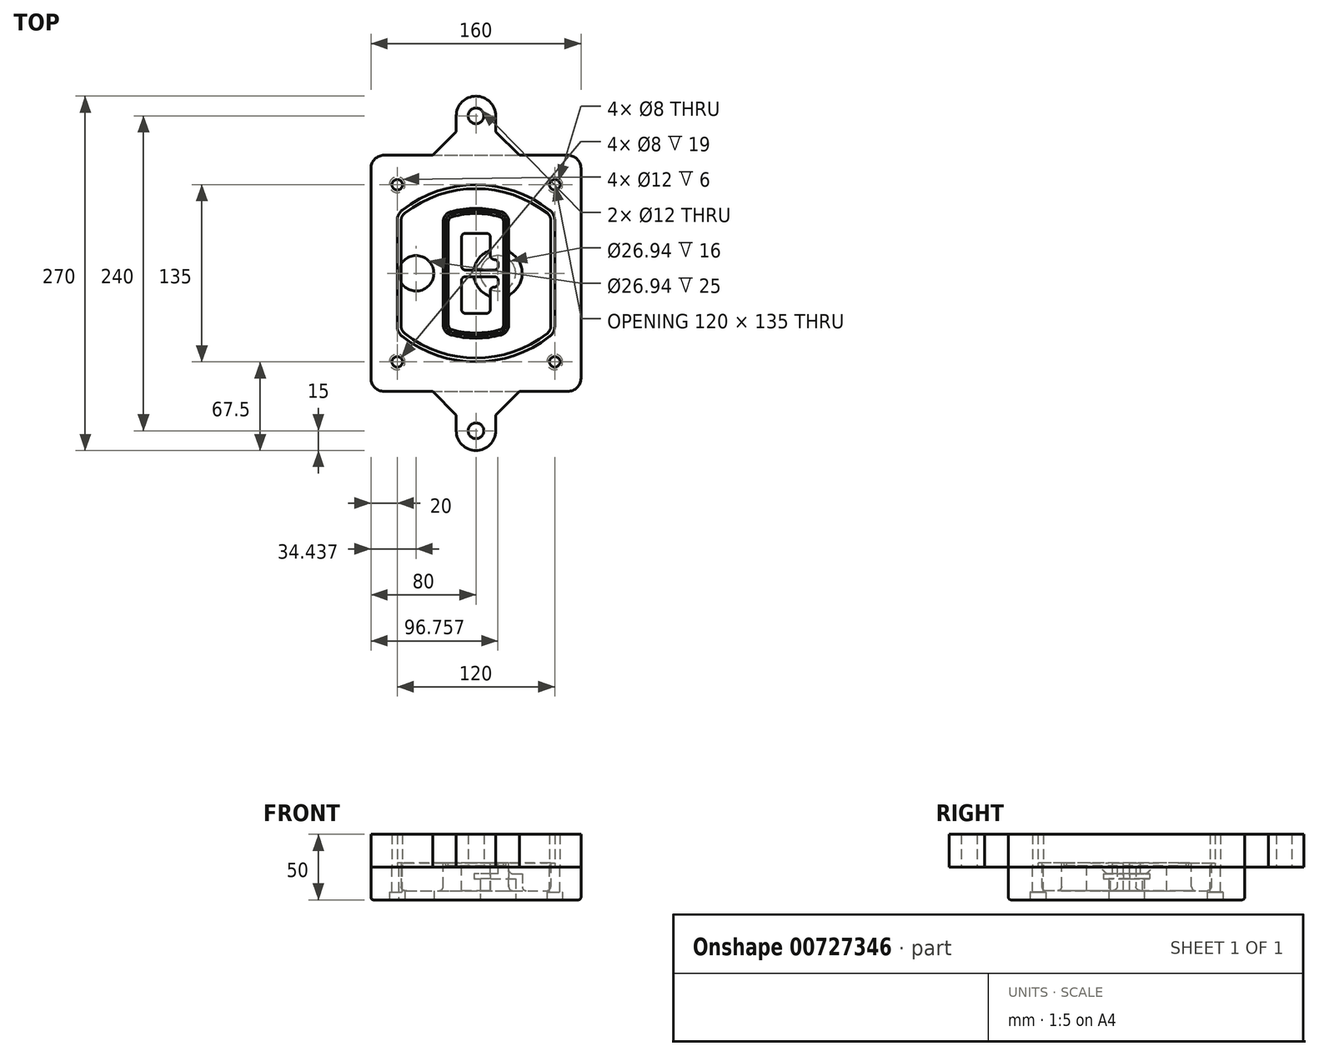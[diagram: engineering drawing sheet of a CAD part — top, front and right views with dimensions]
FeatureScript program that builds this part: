
annotation { "Feature Type Name" : "Feature", "Feature Type Description" : "" }
export const myFeature = defineFeature(function(context is Context, id is Id, definition is map)
    precondition{}
    {
        {
            var Q0;
            Q0=qCreatedBy(makeId("Top.planeOp"),FACE);
            var sketch = newSketch(context, id + "F0", { "sketchPlane" : qUnion([Q0])});
            skPoint(sketch, "E0.rect.middle", {"position": v(0, 0) * mm});
            skLineSegment(sketch, "E1.bottom", {"start": v(-70, -90) * mm, "end": v(70, -90) * mm});
            skLineSegment(sketch, "E1.top", {"start": v(-70, 90) * mm, "end": v(70, 90) * mm});
            skLineSegment(sketch, "E1.left", {"start": v(-80, -80) * mm, "end": v(-80, 80) * mm});
            skLineSegment(sketch, "E1.right", {"start": v(80, -80) * mm, "end": v(80, 80) * mm});
            skLineSegment(sketch, "E2", {"start": v(-80, 90) * mm, "end": v(80, -90) * mm, "construction": true});
            skLineSegment(sketch, "E3", {"start": v(80, 90) * mm, "end": v(-80, -90) * mm, "construction": true});
            skCircle(sketch, "E4", {"center": v(-60, 67.5) * mm, "radius": 4 * mm});
            skCircle(sketch, "E5", {"center": v(60, 67.5) * mm, "radius": 4 * mm});
            skCircle(sketch, "E6", {"center": v(60, -67.5) * mm, "radius": 4 * mm});
            skCircle(sketch, "E7", {"center": v(-60, -67.5) * mm, "radius": 4 * mm});
            skLineSegment(sketch, "E8", {"start": v(-60, 67.5) * mm, "end": v(60, 67.5) * mm, "construction": true});
            skLineSegment(sketch, "E9", {"start": v(60, 67.5) * mm, "end": v(60, -67.5) * mm, "construction": true});
            skLineSegment(sketch, "E10", {"start": v(60, -67.5) * mm, "end": v(-60, -67.5) * mm, "construction": true});
            skLineSegment(sketch, "E11", {"start": v(-60, -67.5) * mm, "end": v(-60, 67.5) * mm, "construction": true});
            skLineSegment(sketch, "E12", {"start": v(-60, 40.3) * mm, "end": v(-60, -40.3) * mm});
            skLineSegment(sketch, "E13", {"start": v(60, 40.3) * mm, "end": v(60, -40.3) * mm});
            skArc(sketch, "E14", {"start": v(56.15, 48.18) * mm, "mid": v(0, 67.5) * mm, "end": v(-56.15, 48.18) * mm});
            skArc(sketch, "E15", {"start": v(-56.15, -48.18) * mm, "mid": v(0, -67.5) * mm, "end": v(56.15, -48.18) * mm});
            skLineSegment(sketch, "E16", {"start": v(-60, 0) * mm, "end": v(60, 0) * mm, "construction": true});
            skPoint(sketch, "E17.visualSharp", {"position": v(-60, -45) * mm});
            skArc(sketch, "E17.filletArc", {"start": v(-60, -40.3) * mm, "mid": v(-58.99, -44.68) * mm, "end": v(-56.15, -48.18) * mm});
            skPoint(sketch, "E18.visualSharp", {"position": v(-60, 45) * mm});
            skArc(sketch, "E18.filletArc", {"start": v(-56.15, 48.18) * mm, "mid": v(-58.99, 44.68) * mm, "end": v(-60, 40.3) * mm});
            skPoint(sketch, "E19.visualSharp", {"position": v(60, 45) * mm});
            skArc(sketch, "E19.filletArc", {"start": v(60, 40.3) * mm, "mid": v(58.99, 44.68) * mm, "end": v(56.15, 48.18) * mm});
            skPoint(sketch, "E20.visualSharp", {"position": v(60, -45) * mm});
            skArc(sketch, "E20.filletArc", {"start": v(56.15, -48.18) * mm, "mid": v(58.99, -44.68) * mm, "end": v(60, -40.3) * mm});
            skPoint(sketch, "E21.visualSharp", {"position": v(-80, 90) * mm});
            skArc(sketch, "E21.filletArc", {"start": v(-70, 90) * mm, "mid": v(-77.07, 87.07) * mm, "end": v(-80, 80) * mm});
            skPoint(sketch, "E22.visualSharp", {"position": v(80, 90) * mm});
            skArc(sketch, "E22.filletArc", {"start": v(80, 80) * mm, "mid": v(77.07, 87.07) * mm, "end": v(70, 90) * mm});
            skPoint(sketch, "E23.visualSharp", {"position": v(80, -90) * mm});
            skArc(sketch, "E23.filletArc", {"start": v(70, -90) * mm, "mid": v(77.07, -87.07) * mm, "end": v(80, -80) * mm});
            skPoint(sketch, "E24.visualSharp", {"position": v(-80, -90) * mm});
            skArc(sketch, "E24.filletArc", {"start": v(-80, -80) * mm, "mid": v(-77.07, -87.07) * mm, "end": v(-70, -90) * mm});
            skArc(sketch, "E25.0", {"start": v(57, 40.3) * mm, "mid": v(56.3, 43.36) * mm, "end": v(54.3, 45.81) * mm});
            skLineSegment(sketch, "E25.1", {"start": v(57, 40.3) * mm, "end": v(57, -40.3) * mm});
            skArc(sketch, "E25.2", {"start": v(54.3, -45.81) * mm, "mid": v(56.3, -43.36) * mm, "end": v(57, -40.3) * mm});
            skArc(sketch, "E25.3", {"start": v(-54.3, -45.81) * mm, "mid": v(0, -64.5) * mm, "end": v(54.3, -45.81) * mm});
            skArc(sketch, "E25.4", {"start": v(-57, -40.3) * mm, "mid": v(-56.3, -43.36) * mm, "end": v(-54.3, -45.81) * mm});
            skArc(sketch, "E25.5", {"start": v(54.3, 45.81) * mm, "mid": v(0, 64.5) * mm, "end": v(-54.3, 45.81) * mm});
            skLineSegment(sketch, "E25.6", {"start": v(-57, 40.3) * mm, "end": v(-57, -40.3) * mm});
            skArc(sketch, "E25.7", {"start": v(-54.3, 45.81) * mm, "mid": v(-56.3, 43.36) * mm, "end": v(-57, 40.3) * mm});
            skArc(sketch, "E26.0", {"start": v(-58.62, 51.33) * mm, "mid": v(-62.58, 46.43) * mm, "end": v(-64, 40.3) * mm});
            skArc(sketch, "E26.1", {"start": v(58.62, 51.33) * mm, "mid": v(0, 71.5) * mm, "end": v(-58.62, 51.33) * mm});
            skArc(sketch, "E26.2", {"start": v(64, 40.3) * mm, "mid": v(62.58, 46.43) * mm, "end": v(58.62, 51.33) * mm});
            skLineSegment(sketch, "E26.3", {"start": v(64, 40.3) * mm, "end": v(64, -40.3) * mm});
            skArc(sketch, "E26.4", {"start": v(58.62, -51.33) * mm, "mid": v(62.58, -46.43) * mm, "end": v(64, -40.3) * mm});
            skLineSegment(sketch, "E26.5", {"start": v(-64, 40.3) * mm, "end": v(-64, -40.3) * mm});
            skArc(sketch, "E26.6", {"start": v(-58.62, -51.33) * mm, "mid": v(0, -71.5) * mm, "end": v(58.62, -51.33) * mm});
            skArc(sketch, "E26.7", {"start": v(-64, -40.3) * mm, "mid": v(-62.58, -46.43) * mm, "end": v(-58.62, -51.33) * mm});
            skSolve(sketch);
        }
        {
            var Q0;
            Q0=makeQuery(id+"F0.imprint","IMPRINT",FACE,{"disambiguationData":[TD([[makeQuery(id+"F0.imprint","IMPRINT",EDGE,{"derivedFrom":sQuery(id+"F0.wireOp",EDGE,"E1.bottom")}),1.0]])]});
            var Q1;
            Q1=makeQuery(id+"F0.imprint","IMPRINT",FACE,{"disambiguationData":[TD([[makeQuery(id+"F0.imprint","IMPRINT",EDGE,{"derivedFrom":sQuery(id+"F0.wireOp",EDGE,"E12")}),1.0]])]});
            var Q2;
            Q2=makeQuery(id+"F0.imprint","IMPRINT",FACE,{"disambiguationData":[TD([[makeQuery(id+"F0.imprint","IMPRINT",EDGE,{"derivedFrom":sQuery(id+"F0.wireOp",EDGE,"E25.0")}),1.0]])]});
            var Q3;
            Q3=makeQuery(id+"F0.imprint","IMPRINT",FACE,{"disambiguationData":[TD([[makeQuery(id+"F0.imprint","IMPRINT",EDGE,{"derivedFrom":sQuery(id+"F0.wireOp",EDGE,"E12")}),-1.0]])]});
            extrude(context, id + "F1", {"entities" : qUnion([Q0, Q1, Q2, Q3]), "oppositeDirection" : true, "depth" : 25 * mm});
        }
        {
            var Q0;
            Q0=makeQuery(id+"F0.imprint","IMPRINT",FACE,{"disambiguationData":[TD([[makeQuery(id+"F0.imprint","IMPRINT",EDGE,{"derivedFrom":sQuery(id+"F0.wireOp",EDGE,"E12")}),1.0]])]});
            extrude(context, id + "F2", {"entities" : qUnion([Q0]), "operationType" : NewBodyOperationType.ADD, "depth" : 3 * mm});
        }
        {
            var Q0;
            Q0=makeQuery(id+"F0.imprint","IMPRINT",FACE,{"disambiguationData":[TD([[makeQuery(id+"F0.imprint","IMPRINT",EDGE,{"derivedFrom":sQuery(id+"F0.wireOp",EDGE,"E25.0")}),1.0]])]});
            extrude(context, id + "F3", {"entities" : qUnion([Q0]), "operationType" : NewBodyOperationType.REMOVE, "oppositeDirection" : true, "depth" : 18 * mm});
        }
        {
            var Q0;
            Q0=makeQuery(id+"F2.opExtrude","CAP_FACE",FACE,{"disambiguationData":[OSD([sQuery(id+"F0.wireOp",EDGE,"E12"),sQuery(id+"F0.wireOp",EDGE,"E13"),sQuery(id+"F0.wireOp",EDGE,"E14"),sQuery(id+"F0.wireOp",EDGE,"E15"),sQuery(id+"F0.wireOp",EDGE,"E17.filletArc"),sQuery(id+"F0.wireOp",EDGE,"E18.filletArc"),sQuery(id+"F0.wireOp",EDGE,"E19.filletArc"),sQuery(id+"F0.wireOp",EDGE,"E20.filletArc"),sQuery(id+"F0.wireOp",EDGE,"E25.0"),sQuery(id+"F0.wireOp",EDGE,"E25.1"),sQuery(id+"F0.wireOp",EDGE,"E25.2"),sQuery(id+"F0.wireOp",EDGE,"E25.3"),sQuery(id+"F0.wireOp",EDGE,"E25.4"),sQuery(id+"F0.wireOp",EDGE,"E25.5"),sQuery(id+"F0.wireOp",EDGE,"E25.6"),sQuery(id+"F0.wireOp",EDGE,"E25.7")])],"isStart":false});
            var sketch = newSketch(context, id + "F4", { "sketchPlane" : qUnion([Q0])});
            skArc(sketch, "E27.0", {"start": v(-19.08, -46.97) * mm, "mid": v(0, -49.5) * mm, "end": v(19.08, -46.97) * mm});
            skArc(sketch, "E28.0", {"start": v(19.08, 46.97) * mm, "mid": v(0, 49.5) * mm, "end": v(-19.08, 46.97) * mm});
            skLineSegment(sketch, "E29", {"start": v(-25, 39.25) * mm, "end": v(-25, -39.25) * mm});
            skLineSegment(sketch, "E30", {"start": v(25, 39.25) * mm, "end": v(25, -39.25) * mm});
            skLineSegment(sketch, "E31", {"start": v(-25, 45.1) * mm, "end": v(25, 45.1) * mm, "construction": true});
            skLineSegment(sketch, "E32", {"start": v(-25, -45.1) * mm, "end": v(25, -45.1) * mm, "construction": true});
            skPoint(sketch, "E33.visualSharp", {"position": v(-25, 45.1) * mm});
            skArc(sketch, "E33.filletArc", {"start": v(-19.08, 46.97) * mm, "mid": v(-23.35, 44.11) * mm, "end": v(-25, 39.25) * mm});
            skPoint(sketch, "E34.visualSharp", {"position": v(25, 45.1) * mm});
            skArc(sketch, "E34.filletArc", {"start": v(25, 39.25) * mm, "mid": v(23.35, 44.11) * mm, "end": v(19.08, 46.97) * mm});
            skPoint(sketch, "E35.visualSharp", {"position": v(25, -45.1) * mm});
            skArc(sketch, "E35.filletArc", {"start": v(19.08, -46.97) * mm, "mid": v(23.35, -44.11) * mm, "end": v(25, -39.25) * mm});
            skPoint(sketch, "E36.visualSharp", {"position": v(-25, -45.1) * mm});
            skArc(sketch, "E36.filletArc", {"start": v(-25, -39.25) * mm, "mid": v(-23.35, -44.11) * mm, "end": v(-19.08, -46.97) * mm});
            skArc(sketch, "E37.0", {"start": v(54.3, 45.81) * mm, "mid": v(0, 64.5) * mm, "end": v(-54.3, 45.81) * mm});
            skArc(sketch, "E37.1", {"start": v(-54.3, 45.81) * mm, "mid": v(-56.3, 43.36) * mm, "end": v(-57, 40.3) * mm});
            skLineSegment(sketch, "E37.2", {"start": v(-57, 40.3) * mm, "end": v(-57, -40.3) * mm});
            skArc(sketch, "E37.3", {"start": v(-57, -40.3) * mm, "mid": v(-56.3, -43.36) * mm, "end": v(-54.3, -45.81) * mm});
            skArc(sketch, "E37.4", {"start": v(-54.3, -45.81) * mm, "mid": v(0, -64.5) * mm, "end": v(54.3, -45.81) * mm});
            skArc(sketch, "E37.5", {"start": v(54.3, -45.81) * mm, "mid": v(56.3, -43.36) * mm, "end": v(57, -40.3) * mm});
            skLineSegment(sketch, "E37.6", {"start": v(57, 40.3) * mm, "end": v(57, -40.3) * mm});
            skArc(sketch, "E37.7", {"start": v(57, 40.3) * mm, "mid": v(56.3, 43.36) * mm, "end": v(54.3, 45.81) * mm});
            skLineSegment(sketch, "E38.0", {"start": v(23, 39.25) * mm, "end": v(23, -39.25) * mm});
            skArc(sketch, "E38.1", {"start": v(18.56, -45.04) * mm, "mid": v(21.76, -42.9) * mm, "end": v(23, -39.25) * mm});
            skArc(sketch, "E38.2", {"start": v(-18.56, -45.04) * mm, "mid": v(0, -47.5) * mm, "end": v(18.56, -45.04) * mm});
            skArc(sketch, "E38.3", {"start": v(-23, -39.25) * mm, "mid": v(-21.76, -42.9) * mm, "end": v(-18.56, -45.04) * mm});
            skLineSegment(sketch, "E38.4", {"start": v(-23, 39.25) * mm, "end": v(-23, -39.25) * mm});
            skArc(sketch, "E38.5", {"start": v(23, 39.25) * mm, "mid": v(21.76, 42.9) * mm, "end": v(18.56, 45.04) * mm});
            skArc(sketch, "E38.6", {"start": v(-18.56, 45.04) * mm, "mid": v(-21.76, 42.9) * mm, "end": v(-23, 39.25) * mm});
            skArc(sketch, "E38.7", {"start": v(18.56, 45.04) * mm, "mid": v(0, 47.5) * mm, "end": v(-18.56, 45.04) * mm});
            skArc(sketch, "E39.0", {"start": v(21, 39.25) * mm, "mid": v(20.18, 41.68) * mm, "end": v(18.04, 43.1) * mm});
            skLineSegment(sketch, "E39.1", {"start": v(21, 39.25) * mm, "end": v(21, -39.25) * mm});
            skArc(sketch, "E39.2", {"start": v(18.04, -43.1) * mm, "mid": v(20.18, -41.68) * mm, "end": v(21, -39.25) * mm});
            skArc(sketch, "E39.3", {"start": v(-18.04, -43.1) * mm, "mid": v(0, -45.5) * mm, "end": v(18.04, -43.1) * mm});
            skArc(sketch, "E39.4", {"start": v(-21, -39.25) * mm, "mid": v(-20.18, -41.68) * mm, "end": v(-18.04, -43.1) * mm});
            skArc(sketch, "E39.5", {"start": v(18.04, 43.1) * mm, "mid": v(0, 45.5) * mm, "end": v(-18.04, 43.1) * mm});
            skLineSegment(sketch, "E39.6", {"start": v(-21, 39.25) * mm, "end": v(-21, -39.25) * mm});
            skArc(sketch, "E39.7", {"start": v(-18.04, 43.1) * mm, "mid": v(-20.18, 41.68) * mm, "end": v(-21, 39.25) * mm});
            skLineSegment(sketch, "E40", {"start": v(-25, 0) * mm, "end": v(25, 0) * mm, "construction": true});
            skLineSegment(sketch, "E41", {"start": v(-11, 5.5) * mm, "end": v(-11, 27.5) * mm});
            skLineSegment(sketch, "E42", {"start": v(-8, 30.5) * mm, "end": v(8, 30.5) * mm});
            skLineSegment(sketch, "E43", {"start": v(11, 27.5) * mm, "end": v(11, 13.5) * mm});
            skLineSegment(sketch, "E44", {"start": v(14, 10.5) * mm, "end": v(14, 10.5) * mm});
            skLineSegment(sketch, "E45", {"start": v(17, 7.5) * mm, "end": v(17, 5.5) * mm});
            skLineSegment(sketch, "E46", {"start": v(14, 2.5) * mm, "end": v(-8, 2.5) * mm});
            skPoint(sketch, "E47.visualSharp", {"position": v(-11, 30.5) * mm});
            skArc(sketch, "E47.filletArc", {"start": v(-8, 30.5) * mm, "mid": v(-10.12, 29.62) * mm, "end": v(-11, 27.5) * mm});
            skPoint(sketch, "E48.visualSharp", {"position": v(11, 30.5) * mm});
            skArc(sketch, "E48.filletArc", {"start": v(11, 27.5) * mm, "mid": v(10.12, 29.62) * mm, "end": v(8, 30.5) * mm});
            skPoint(sketch, "E49.visualSharp", {"position": v(11, 10.5) * mm});
            skArc(sketch, "E49.filletArc", {"start": v(11, 13.5) * mm, "mid": v(11.88, 11.38) * mm, "end": v(14, 10.5) * mm});
            skPoint(sketch, "E50.visualSharp", {"position": v(17, 10.5) * mm});
            skArc(sketch, "E50.filletArc", {"start": v(17, 7.5) * mm, "mid": v(16.12, 9.62) * mm, "end": v(14, 10.5) * mm});
            skPoint(sketch, "E51.visualSharp", {"position": v(17, 2.5) * mm});
            skArc(sketch, "E51.filletArc", {"start": v(14, 2.5) * mm, "mid": v(16.12, 3.38) * mm, "end": v(17, 5.5) * mm});
            skPoint(sketch, "E52.visualSharp", {"position": v(-11, 2.5) * mm});
            skArc(sketch, "E52.filletArc", {"start": v(-11, 5.5) * mm, "mid": v(-10.12, 3.38) * mm, "end": v(-8, 2.5) * mm});
            skLineSegment(sketch, "E53.0.MirrorCS", {"start": v(14, -2.5) * mm, "end": v(-8, -2.5) * mm});
            skArc(sketch, "E54.0.MirrorCS", {"start": v(-11, -5.5) * mm, "mid": v(-10.12, -3.38) * mm, "end": v(-8, -2.5) * mm});
            skLineSegment(sketch, "E55.0.MirrorCS", {"start": v(-11, -5.5) * mm, "end": v(-11, -27.5) * mm});
            skArc(sketch, "E56.0.MirrorCS", {"start": v(-8, -30.5) * mm, "mid": v(-10.12, -29.62) * mm, "end": v(-11, -27.5) * mm});
            skLineSegment(sketch, "E57.0.MirrorCS", {"start": v(-8, -30.5) * mm, "end": v(8, -30.5) * mm});
            skArc(sketch, "E58.0.MirrorCS", {"start": v(11, -27.5) * mm, "mid": v(10.12, -29.62) * mm, "end": v(8, -30.5) * mm});
            skLineSegment(sketch, "E59.0.MirrorCS", {"start": v(11, -27.5) * mm, "end": v(11, -13.5) * mm});
            skArc(sketch, "E60.0.MirrorCS", {"start": v(11, -13.5) * mm, "mid": v(11.88, -11.38) * mm, "end": v(14, -10.5) * mm});
            skArc(sketch, "E61.0.MirrorCS", {"start": v(17, -7.5) * mm, "mid": v(16.12, -9.62) * mm, "end": v(14, -10.5) * mm});
            skLineSegment(sketch, "E62.0.MirrorCS", {"start": v(17, -7.5) * mm, "end": v(17, -5.5) * mm});
            skArc(sketch, "E63.0.MirrorCS", {"start": v(14, -2.5) * mm, "mid": v(16.12, -3.38) * mm, "end": v(17, -5.5) * mm});
            skSolve(sketch);
        }
        {
            var Q0;
            Q0=makeQuery(id+"F4.imprint","IMPRINT",FACE,{"disambiguationData":[TD([[makeQuery(id+"F4.imprint","IMPRINT",EDGE,{"derivedFrom":sQuery(id+"F4.wireOp",EDGE,"E27.0")}),1.0]])]});
            var Q1;
            Q1=makeQuery(id+"F4.imprint","IMPRINT",FACE,{"disambiguationData":[TD([[makeQuery(id+"F4.imprint","IMPRINT",EDGE,{"derivedFrom":sQuery(id+"F4.wireOp",EDGE,"E38.0")}),-1.0]])]});
            var Q2;
            Q2=makeQuery(id+"F4.imprint","IMPRINT",FACE,{"disambiguationData":[TD([[makeQuery(id+"F4.imprint","IMPRINT",EDGE,{"derivedFrom":sQuery(id+"F4.wireOp",EDGE,"E39.0")}),1.0]])]});
            extrude(context, id + "F5", {"entities" : qUnion([Q0, Q1, Q2]), "operationType" : NewBodyOperationType.ADD, "endBound" : BoundingType.UP_TO_NEXT, "oppositeDirection" : true, "depth" : 25 * mm});
        }
        {
            var Q0;
            Q0=makeQuery(id+"F4.imprint","IMPRINT",FACE,{"disambiguationData":[TD([[makeQuery(id+"F4.imprint","IMPRINT",EDGE,{"derivedFrom":sQuery(id+"F4.wireOp",EDGE,"E38.0")}),-1.0]])]});
            extrude(context, id + "F6", {"entities" : qUnion([Q0]), "operationType" : NewBodyOperationType.REMOVE, "oppositeDirection" : true, "depth" : 2 * mm});
        }
        {
            var Q0;
            Q0=makeQuery(id+"F1.opExtrude","CAP_FACE",FACE,{"disambiguationData":[OSD([sQuery(id+"F0.wireOp",EDGE,"E1.bottom"),sQuery(id+"F0.wireOp",EDGE,"E1.top"),sQuery(id+"F0.wireOp",EDGE,"E1.left"),sQuery(id+"F0.wireOp",EDGE,"E1.right"),sQuery(id+"F0.wireOp",EDGE,"E4"),sQuery(id+"F0.wireOp",EDGE,"E5"),sQuery(id+"F0.wireOp",EDGE,"E6"),sQuery(id+"F0.wireOp",EDGE,"E7"),sQuery(id+"F0.wireOp",EDGE,"E21.filletArc"),sQuery(id+"F0.wireOp",EDGE,"E22.filletArc"),sQuery(id+"F0.wireOp",EDGE,"E23.filletArc"),sQuery(id+"F0.wireOp",EDGE,"E24.filletArc")])],"isStart":false});
            var sketch = newSketch(context, id + "F7", { "sketchPlane" : qUnion([Q0])});
            skCircle(sketch, "E64", {"center": v(16.76, 0) * mm, "radius": 13.47 * mm});
            skCircle(sketch, "E65", {"center": v(-45.56, 0) * mm, "radius": 13.47 * mm});
            skLineSegment(sketch, "E66", {"start": v(80, 0) * mm, "end": v(-80, 0) * mm});
            skCircle(sketch, "E67", {"center": v(16.76, 0) * mm, "radius": 18.47 * mm});
            skCircle(sketch, "E68", {"center": v(60, -67.5) * mm, "radius": 6 * mm});
            skCircle(sketch, "E69", {"center": v(-60, -67.5) * mm, "radius": 6 * mm});
            skCircle(sketch, "E70", {"center": v(-60, 67.5) * mm, "radius": 6 * mm});
            skCircle(sketch, "E71", {"center": v(60, 67.5) * mm, "radius": 6 * mm});
            skSolve(sketch);
        }
        {
            var Q0;
            {var subQ1=sQuery(id+"F7.wireOp",EDGE,"E66");var subQ4=sQuery(id+"F7.wireOp",EDGE,"E64");var subQ6=makeQuery(id+"F7.imprint","INTERSECT",VERTEX,{"disambiguationData":[OD(0.0)],"derivedFrom":[subQ4,subQ1]});Q0=makeQuery(id+"F7.imprint","IMPRINT",FACE,{"disambiguationData":[TD([[makeQuery(id+"F7.imprint","IMPRINT",EDGE,{"disambiguationData":[TD([[subQ6,-1.0]])],"derivedFrom":subQ4}),-1.0]])]});}
            var Q1;
            {var subQ0=sQuery(id+"F7.wireOp",EDGE,"E66");var subQ1=sQuery(id+"F7.wireOp",EDGE,"E64");var subQ3=makeQuery(id+"F7.imprint","INTERSECT",VERTEX,{"disambiguationData":[OD(0.0)],"derivedFrom":[subQ1,subQ0]});Q1=makeQuery(id+"F7.imprint","IMPRINT",FACE,{"disambiguationData":[TD([[makeQuery(id+"F7.imprint","IMPRINT",EDGE,{"disambiguationData":[TD([[subQ3,-1.0]])],"derivedFrom":subQ1}),1.0]])]});}
            var Q2;
            {var subQ0=sQuery(id+"F7.wireOp",EDGE,"E66");var subQ1=sQuery(id+"F7.wireOp",EDGE,"E64");var subQ3=makeQuery(id+"F7.imprint","INTERSECT",VERTEX,{"disambiguationData":[OD(0.0)],"derivedFrom":[subQ1,subQ0]});Q2=makeQuery(id+"F7.imprint","IMPRINT",FACE,{"disambiguationData":[TD([[makeQuery(id+"F7.imprint","IMPRINT",EDGE,{"disambiguationData":[TD([[subQ3,1.0]])],"derivedFrom":subQ1}),1.0]])]});}
            var Q3;
            {var subQ1=sQuery(id+"F7.wireOp",EDGE,"E66");var subQ4=sQuery(id+"F7.wireOp",EDGE,"E64");var subQ6=makeQuery(id+"F7.imprint","INTERSECT",VERTEX,{"disambiguationData":[OD(0.0)],"derivedFrom":[subQ4,subQ1]});Q3=makeQuery(id+"F7.imprint","IMPRINT",FACE,{"disambiguationData":[TD([[makeQuery(id+"F7.imprint","IMPRINT",EDGE,{"disambiguationData":[TD([[subQ6,1.0]])],"derivedFrom":subQ4}),-1.0]])]});}
            extrude(context, id + "F8", {"entities" : qUnion([Q0, Q1, Q2, Q3]), "operationType" : NewBodyOperationType.ADD, "oppositeDirection" : true, "depth" : 20 * mm});
        }
        {
            var Q0;
            {var subQ0=sQuery(id+"F7.wireOp",EDGE,"E66");var subQ1=sQuery(id+"F7.wireOp",EDGE,"E64");var subQ3=makeQuery(id+"F7.imprint","INTERSECT",VERTEX,{"disambiguationData":[OD(0.0)],"derivedFrom":[subQ1,subQ0]});Q0=makeQuery(id+"F7.imprint","IMPRINT",FACE,{"disambiguationData":[TD([[makeQuery(id+"F7.imprint","IMPRINT",EDGE,{"disambiguationData":[TD([[subQ3,-1.0]])],"derivedFrom":subQ1}),1.0]])]});}
            var Q1;
            {var subQ0=sQuery(id+"F7.wireOp",EDGE,"E66");var subQ1=sQuery(id+"F7.wireOp",EDGE,"E64");var subQ3=makeQuery(id+"F7.imprint","INTERSECT",VERTEX,{"disambiguationData":[OD(0.0)],"derivedFrom":[subQ1,subQ0]});Q1=makeQuery(id+"F7.imprint","IMPRINT",FACE,{"disambiguationData":[TD([[makeQuery(id+"F7.imprint","IMPRINT",EDGE,{"disambiguationData":[TD([[subQ3,1.0]])],"derivedFrom":subQ1}),1.0]])]});}
            extrude(context, id + "F9", {"entities" : qUnion([Q0, Q1]), "operationType" : NewBodyOperationType.REMOVE, "oppositeDirection" : true, "depth" : 16 * mm});
        }
        {
            var Q0;
            {var subQ0=sQuery(id+"F7.wireOp",EDGE,"E66");var subQ1=sQuery(id+"F7.wireOp",EDGE,"E65");var subQ3=makeQuery(id+"F7.imprint","INTERSECT",VERTEX,{"disambiguationData":[OD(0.0)],"derivedFrom":[subQ1,subQ0]});Q0=makeQuery(id+"F7.imprint","IMPRINT",FACE,{"disambiguationData":[TD([[makeQuery(id+"F7.imprint","IMPRINT",EDGE,{"disambiguationData":[TD([[subQ3,-1.0]])],"derivedFrom":subQ1}),1.0]])]});}
            var Q1;
            {var subQ0=sQuery(id+"F7.wireOp",EDGE,"E66");var subQ1=sQuery(id+"F7.wireOp",EDGE,"E65");var subQ3=makeQuery(id+"F7.imprint","INTERSECT",VERTEX,{"disambiguationData":[OD(0.0)],"derivedFrom":[subQ1,subQ0]});Q1=makeQuery(id+"F7.imprint","IMPRINT",FACE,{"disambiguationData":[TD([[makeQuery(id+"F7.imprint","IMPRINT",EDGE,{"disambiguationData":[TD([[subQ3,1.0]])],"derivedFrom":subQ1}),1.0]])]});}
            extrude(context, id + "F10", {"entities" : qUnion([Q0, Q1]), "operationType" : NewBodyOperationType.REMOVE, "oppositeDirection" : true, "depth" : 25 * mm});
        }
        {
            var Q0;
            Q0=makeQuery(id+"F7.imprint","IMPRINT",FACE,{"disambiguationData":[TD([[makeQuery(id+"F7.imprint","IMPRINT",EDGE,{"derivedFrom":sQuery(id+"F7.wireOp",EDGE,"E68")}),1.0]])]});
            var Q1;
            Q1=makeQuery(id+"F7.imprint","IMPRINT",FACE,{"disambiguationData":[TD([[makeQuery(id+"F7.imprint","IMPRINT",EDGE,{"derivedFrom":makeQuery(id+"F1.opExtrude","CAP_EDGE",EDGE,{"disambiguationData":[OSD([sQuery(id+"F0.wireOp",EDGE,"E5")])],"isStart":false})}),-1.0]])]});
            var Q2;
            Q2=makeQuery(id+"F7.imprint","IMPRINT",FACE,{"disambiguationData":[TD([[makeQuery(id+"F7.imprint","IMPRINT",EDGE,{"derivedFrom":sQuery(id+"F7.wireOp",EDGE,"E69")}),1.0]])]});
            var Q3;
            Q3=makeQuery(id+"F7.imprint","IMPRINT",FACE,{"disambiguationData":[TD([[makeQuery(id+"F7.imprint","IMPRINT",EDGE,{"derivedFrom":makeQuery(id+"F1.opExtrude","CAP_EDGE",EDGE,{"disambiguationData":[OSD([sQuery(id+"F0.wireOp",EDGE,"E4")])],"isStart":false})}),-1.0]])]});
            var Q4;
            Q4=makeQuery(id+"F7.imprint","IMPRINT",FACE,{"disambiguationData":[TD([[makeQuery(id+"F7.imprint","IMPRINT",EDGE,{"derivedFrom":sQuery(id+"F7.wireOp",EDGE,"E70")}),1.0]])]});
            var Q5;
            Q5=makeQuery(id+"F7.imprint","IMPRINT",FACE,{"disambiguationData":[TD([[makeQuery(id+"F7.imprint","IMPRINT",EDGE,{"derivedFrom":makeQuery(id+"F1.opExtrude","CAP_EDGE",EDGE,{"disambiguationData":[OSD([sQuery(id+"F0.wireOp",EDGE,"E7")])],"isStart":false})}),-1.0]])]});
            var Q6;
            Q6=makeQuery(id+"F7.imprint","IMPRINT",FACE,{"disambiguationData":[TD([[makeQuery(id+"F7.imprint","IMPRINT",EDGE,{"derivedFrom":sQuery(id+"F7.wireOp",EDGE,"E71")}),1.0]])]});
            var Q7;
            Q7=makeQuery(id+"F7.imprint","IMPRINT",FACE,{"disambiguationData":[TD([[makeQuery(id+"F7.imprint","IMPRINT",EDGE,{"derivedFrom":makeQuery(id+"F1.opExtrude","CAP_EDGE",EDGE,{"disambiguationData":[OSD([sQuery(id+"F0.wireOp",EDGE,"E6")])],"isStart":false})}),-1.0]])]});
            extrude(context, id + "F11", {"entities" : qUnion([Q0, Q1, Q2, Q3, Q4, Q5, Q6, Q7]), "operationType" : NewBodyOperationType.REMOVE, "oppositeDirection" : true, "depth" : 6 * mm});
        }
        {
            var Q0;
            Q0=makeQuery(id+"F9.boolean.opBoolean","COPY",FACE,{"derivedFrom":makeQuery(id+"F9.opExtrude","CAP_FACE",FACE,{"disambiguationData":[OSD([sQuery(id+"F7.wireOp",EDGE,"E64")])],"isStart":false})});
            var sketch = newSketch(context, id + "F12", { "sketchPlane" : qUnion([Q0])});
            skArc(sketch, "E72.0", {"start": v(11, 17.55) * mm, "mid": v(2.57, 11.82) * mm, "end": v(-1.54, 2.5) * mm});
            skArc(sketch, "E72.1", {"start": v(-1.54, -2.5) * mm, "mid": v(2.57, -11.82) * mm, "end": v(11, -17.55) * mm});
            skLineSegment(sketch, "E73", {"start": v(-1.54, -2.5) * mm, "end": v(14, -2.5) * mm});
            skLineSegment(sketch, "E74.0", {"start": v(14, 2.5) * mm, "end": v(-1.54, 2.5) * mm});
            skArc(sketch, "E74.1", {"start": v(14, 2.5) * mm, "mid": v(16.12, 3.38) * mm, "end": v(17, 5.5) * mm});
            skLineSegment(sketch, "E74.2", {"start": v(17, 7.5) * mm, "end": v(17, 5.5) * mm});
            skArc(sketch, "E74.3", {"start": v(17, 7.5) * mm, "mid": v(16.12, 9.62) * mm, "end": v(14, 10.5) * mm});
            skArc(sketch, "E74.4", {"start": v(11, 13.5) * mm, "mid": v(11.88, 11.38) * mm, "end": v(14, 10.5) * mm});
            skLineSegment(sketch, "E74.5", {"start": v(11, 17.55) * mm, "end": v(11, 13.5) * mm});
            skLineSegment(sketch, "E74.7", {"start": v(14, -2.5) * mm, "end": v(-1.54, -2.5) * mm});
            skArc(sketch, "E74.8", {"start": v(14, -2.5) * mm, "mid": v(16.12, -3.38) * mm, "end": v(17, -5.5) * mm});
            skLineSegment(sketch, "E74.9", {"start": v(17, -7.5) * mm, "end": v(17, -5.5) * mm});
            skArc(sketch, "E74.10", {"start": v(17, -7.5) * mm, "mid": v(16.12, -9.62) * mm, "end": v(14, -10.5) * mm});
            skArc(sketch, "E74.11", {"start": v(11, -13.5) * mm, "mid": v(11.88, -11.38) * mm, "end": v(14, -10.5) * mm});
            skLineSegment(sketch, "E74.12", {"start": v(11, -17.55) * mm, "end": v(11, -13.5) * mm});
            skPoint(sketch, "E75.orphan", {"position": v(11, -27.5) * mm});
            skPoint(sketch, "E76.orphan", {"position": v(-8, -2.5) * mm});
            skPoint(sketch, "E77.orphan", {"position": v(-8, 2.5) * mm});
            skPoint(sketch, "E78.orphan", {"position": v(11, 27.5) * mm});
            skSolve(sketch);
        }
        {
            var Q0;
            {var subQ7=sQuery(id+"F12.wireOp",EDGE,"E72.0");var subQ14=sQuery(id+"F12.wireOp",EDGE,"E72.1");var subQ16=sQuery(id+"F12.wireOp",EDGE,"E74.1");var subQ18=sQuery(id+"F12.wireOp",EDGE,"E74.8");Q0=qUnion([makeQuery(id+"F12.imprint","IMPRINT",FACE,{"disambiguationData":[TD([[makeQuery(id+"F12.imprint","IMPRINT",EDGE,{"derivedFrom":subQ7}),1.0]])]}),makeQuery(id+"F12.imprint","IMPRINT",FACE,{"disambiguationData":[TD([[makeQuery(id+"F12.imprint","IMPRINT",EDGE,{"derivedFrom":subQ14}),1.0]])]}),makeQuery(id+"F12.imprint","IMPRINT",FACE,{"disambiguationData":[TD([[makeQuery(id+"F12.imprint","IMPRINT",EDGE,{"derivedFrom":subQ16}),1.0]])]}),makeQuery(id+"F12.imprint","IMPRINT",FACE,{"disambiguationData":[TD([[makeQuery(id+"F12.imprint","IMPRINT",EDGE,{"derivedFrom":subQ18}),-1.0]])]})]);}
            var Q1;
            Q1=makeQuery(id+"F5.boolean.opBoolean","SPLIT",FACE,{"disambiguationData":[TD([makeQuery(id+"F5.opExtrude","SWEPT_FACE",FACE,{"disambiguationData":[OSD([sQuery(id+"F4.wireOp",EDGE,"E41")])]})])],"derivedFrom":makeQuery(id+"F3.boolean.opBoolean","COPY",FACE,{"derivedFrom":makeQuery(id+"F3.opExtrude","CAP_FACE",FACE,{"disambiguationData":[OSD([sQuery(id+"F0.wireOp",EDGE,"E25.0"),sQuery(id+"F0.wireOp",EDGE,"E25.1"),sQuery(id+"F0.wireOp",EDGE,"E25.2"),sQuery(id+"F0.wireOp",EDGE,"E25.3"),sQuery(id+"F0.wireOp",EDGE,"E25.4"),sQuery(id+"F0.wireOp",EDGE,"E25.5"),sQuery(id+"F0.wireOp",EDGE,"E25.6"),sQuery(id+"F0.wireOp",EDGE,"E25.7")])],"isStart":false})})});
            extrude(context, id + "F13", {"entities" : qUnion([Q0]), "operationType" : NewBodyOperationType.REMOVE, "endBound" : BoundingType.UP_TO_SURFACE, "endBoundEntityFace" : qUnion([Q1]), "depth" : 25 * mm});
        }
        {
            var Q0;
            Q0=makeQuery(id+"F3.boolean.opBoolean","COPY",EDGE,{"derivedFrom":makeQuery(id+"F3.opExtrude","CAP_EDGE",EDGE,{"disambiguationData":[OSD([sQuery(id+"F0.wireOp",EDGE,"E25.6")])],"isStart":false})});
            var Q1;
            Q1=makeQuery(id+"F8.boolean.opBoolean","INTERSECT",EDGE,{"derivedFrom":[makeQuery(id+"F5.opExtrude","SWEPT_FACE",FACE,{"disambiguationData":[OSD([sQuery(id+"F4.wireOp",EDGE,"E30")])]}),makeQuery(id+"F8.opExtrude","CAP_FACE",FACE,{"disambiguationData":[OSD([sQuery(id+"F7.wireOp",EDGE,"E67")])],"isStart":false})]});
            var Q2;
            Q2=makeQuery(id+"F8.boolean.opBoolean","INTERSECT",EDGE,{"disambiguationData":[OD(1.0)],"derivedFrom":[makeQuery(id+"F5.opExtrude","SWEPT_FACE",FACE,{"disambiguationData":[OSD([sQuery(id+"F4.wireOp",EDGE,"E30")])]}),makeQuery(id+"F8.opExtrude","SWEPT_FACE",FACE,{"disambiguationData":[OSD([sQuery(id+"F7.wireOp",EDGE,"E67")])]})]});
            var Q3;
            {var subQ0=sQuery(id+"F4.wireOp",EDGE,"E30");Q3=makeQuery(id+"F8.boolean.opBoolean","SPLIT",EDGE,{"disambiguationData":[TD([makeQuery(id+"F5.opExtrude","SWEPT_FACE",FACE,{"disambiguationData":[OSD([sQuery(id+"F4.wireOp",EDGE,"E35.filletArc")])]})])],"derivedFrom":makeQuery(id+"F5.opExtrude","CAP_EDGE",EDGE,{"disambiguationData":[OSD([subQ0])],"isStart":false})});}
            var Q4;
            {var subQ0=sQuery(id+"F0.wireOp",EDGE,"E25.7");var subQ1=sQuery(id+"F0.wireOp",EDGE,"E25.1");var subQ2=sQuery(id+"F0.wireOp",EDGE,"E25.6");var subQ3=sQuery(id+"F0.wireOp",EDGE,"E25.5");var subQ4=sQuery(id+"F0.wireOp",EDGE,"E25.4");var subQ5=sQuery(id+"F0.wireOp",EDGE,"E25.0");var subQ6=sQuery(id+"F0.wireOp",EDGE,"E25.2");var subQ7=sQuery(id+"F0.wireOp",EDGE,"E25.3");Q4=makeQuery(id+"F8.boolean.opBoolean","INTERSECT",EDGE,{"derivedFrom":[makeQuery(id+"F5.boolean.opBoolean","SPLIT",FACE,{"disambiguationData":[TD([makeQuery(id+"F2.opExtrude","SWEPT_FACE",FACE,{"disambiguationData":[OSD([subQ5])]})])],"derivedFrom":makeQuery(id+"F3.boolean.opBoolean","COPY",FACE,{"derivedFrom":makeQuery(id+"F3.opExtrude","CAP_FACE",FACE,{"disambiguationData":[OSD([subQ5,subQ1,subQ6,subQ7,subQ4,subQ3,subQ2,subQ0])],"isStart":false})})}),makeQuery(id+"F8.opExtrude","SWEPT_FACE",FACE,{"disambiguationData":[OSD([sQuery(id+"F7.wireOp",EDGE,"E67")])]})]});}
            var Q5;
            Q5=makeQuery(id+"F8.boolean.opBoolean","INTERSECT",EDGE,{"disambiguationData":[OD(0.0)],"derivedFrom":[makeQuery(id+"F5.opExtrude","SWEPT_FACE",FACE,{"disambiguationData":[OSD([sQuery(id+"F4.wireOp",EDGE,"E30")])]}),makeQuery(id+"F8.opExtrude","SWEPT_FACE",FACE,{"disambiguationData":[OSD([sQuery(id+"F7.wireOp",EDGE,"E67")])]})]});
            fillet(context, id + "F14", {"entities" : qUnion([Q0, Q1, Q2, Q3, Q4, Q5]), "radius" : 3 * mm, "tangentPropagation" : true, "allowEdgeOverflow" : false});
        }
        {
            var Q0;
            Q0=makeQuery(id+"F1.opExtrude","CAP_EDGE",EDGE,{"disambiguationData":[OSD([sQuery(id+"F0.wireOp",EDGE,"E1.bottom")])],"isStart":false});
            fillet(context, id + "F15", {"entities" : qUnion([Q0]), "radius" : 2 * mm, "tangentPropagation" : true, "allowEdgeOverflow" : false});
        }
        {
            var Q0;
            {var subQ0=sQuery(id+"F0.wireOp",EDGE,"E21.filletArc");var subQ1=sQuery(id+"F0.wireOp",EDGE,"E7");var subQ2=sQuery(id+"F0.wireOp",EDGE,"E6");var subQ3=sQuery(id+"F0.wireOp",EDGE,"E5");var subQ4=sQuery(id+"F0.wireOp",EDGE,"E4");var subQ5=sQuery(id+"F0.wireOp",EDGE,"E22.filletArc");var subQ6=sQuery(id+"F0.wireOp",EDGE,"E1.bottom");var subQ7=sQuery(id+"F0.wireOp",EDGE,"E1.right");var subQ8=sQuery(id+"F0.wireOp",EDGE,"E1.top");var subQ9=sQuery(id+"F0.wireOp",EDGE,"E1.left");var subQ10=sQuery(id+"F0.wireOp",EDGE,"E23.filletArc");var subQ11=sQuery(id+"F0.wireOp",EDGE,"E24.filletArc");Q0=makeQuery(id+"F2.boolean.opBoolean","SPLIT",FACE,{"disambiguationData":[TD([makeQuery(id+"F1.opExtrude","SWEPT_FACE",FACE,{"disambiguationData":[OSD([subQ6])]})])],"derivedFrom":makeQuery(id+"F1.opExtrude","CAP_FACE",FACE,{"disambiguationData":[OSD([subQ6,subQ8,subQ9,subQ7,subQ4,subQ3,subQ2,subQ1,subQ0,subQ5,subQ10,subQ11])],"isStart":true})});}
            var sketch = newSketch(context, id + "F16", { "sketchPlane" : qUnion([Q0])});
            skLineSegment(sketch, "E79", {"start": v(0, 90) * mm, "end": v(0, 120) * mm, "construction": true});
            skCircle(sketch, "E80", {"center": v(0, 120) * mm, "radius": 6 * mm});
            skLineSegment(sketch, "E81", {"start": v(-33, 90) * mm, "end": v(-15, 108) * mm});
            skLineSegment(sketch, "E82", {"start": v(-15, 108) * mm, "end": v(-15, 120) * mm});
            skLineSegment(sketch, "E83", {"start": v(15, 108) * mm, "end": v(15, 120) * mm});
            skLineSegment(sketch, "E84", {"start": v(15, 108) * mm, "end": v(33, 90) * mm});
            skLineSegment(sketch, "E85", {"start": v(-33, 90) * mm, "end": v(33, 90) * mm});
            skArc(sketch, "E86", {"start": v(15, 120) * mm, "mid": v(0, 135) * mm, "end": v(-15, 120) * mm});
            skLineSegment(sketch, "E87", {"start": v(-80, 0) * mm, "end": v(80, 0) * mm, "construction": true});
            skLineSegment(sketch, "E88.MirrorCS", {"start": v(-15, -108) * mm, "end": v(-15, -120) * mm});
            skLineSegment(sketch, "E89.MirrorCS", {"start": v(-33, -90) * mm, "end": v(-15, -108) * mm});
            skArc(sketch, "E90.MirrorCS", {"start": v(15, -120) * mm, "mid": v(0, -135) * mm, "end": v(-15, -120) * mm});
            skCircle(sketch, "E91.MirrorC", {"center": v(0, -120) * mm, "radius": 6 * mm});
            skLineSegment(sketch, "E92.MirrorCS", {"start": v(0, -90) * mm, "end": v(0, -120) * mm, "construction": true});
            skLineSegment(sketch, "E93.MirrorCS", {"start": v(15, -108) * mm, "end": v(15, -120) * mm});
            skLineSegment(sketch, "E94.MirrorCS", {"start": v(15, -108) * mm, "end": v(33, -90) * mm});
            skSolve(sketch);
        }
        {
            var Q0;
            Q0=makeQuery(id+"F16.imprint","IMPRINT",FACE,{"disambiguationData":[TD([[makeQuery(id+"F16.imprint","IMPRINT",EDGE,{"derivedFrom":sQuery(id+"F16.wireOp",EDGE,"E80")}),-1.0]])]});
            var Q1;
            Q1=makeQuery(id+"F16.imprint","IMPRINT",FACE,{"disambiguationData":[TD([[makeQuery(id+"F16.imprint","IMPRINT",EDGE,{"derivedFrom":sQuery(id+"F16.wireOp",EDGE,"E88.MirrorCS")}),1.0]])]});
            var Q2;
            {var subQ5=sQuery(id+"F16.wireOp",EDGE,"E85");Q2=makeQuery(id+"F16.imprint","IMPRINT",FACE,{"disambiguationData":[TD([[makeQuery(id+"F16.imprint","IMPRINT",EDGE,{"derivedFrom":subQ5}),-1.0]])]});}
            extrude(context, id + "F17", {"entities" : qUnion([Q0, Q1, Q2]), "depth" : 25 * mm, "offsetDistance" : 25 * mm});
        }
    });
